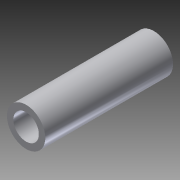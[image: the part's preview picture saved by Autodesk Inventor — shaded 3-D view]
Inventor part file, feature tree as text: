
AUTODESK INVENTOR PART (.ipt)
format: ipt  version: 2016 (Build 200138000, 138)  size: 80,896 bytes
history: native  units: mm
features: extrude x1, sketch x1
ambient origin geometry x8: Origin, YZ Plane, XZ Plane, XY Plane, X Axis, Y Axis, Z Axis, Center Point
bodies: Solid1 (feature_tree)
feature tree (2):
  extrude  "Extrusion1"  Depth=10.0mm
  sketch  "Sketch1"  dims[d0=2.0mm d1=3.0mm d2=10.0mm d3=0.0mm]
